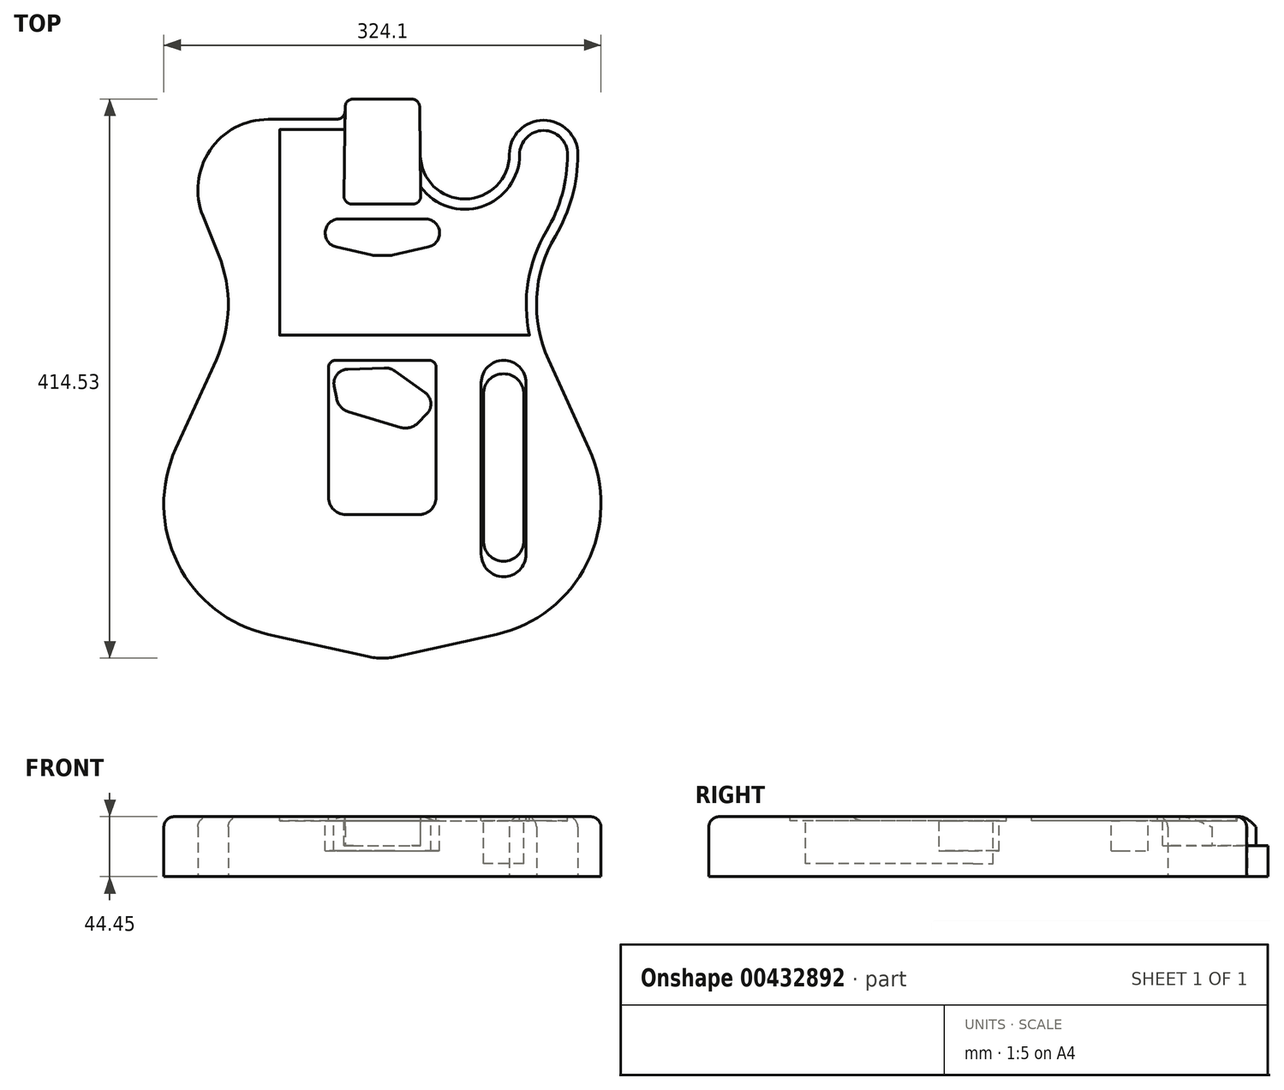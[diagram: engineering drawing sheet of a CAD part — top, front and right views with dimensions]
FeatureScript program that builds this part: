
annotation { "Feature Type Name" : "Feature", "Feature Type Description" : "" }
export const myFeature = defineFeature(function(context is Context, id is Id, definition is map)
    precondition{}
    {
        {
            var Q0;
            Q0=qCreatedBy(makeId("Top.planeOp"),FACE);
            var sketch = newSketch(context, id + "F0", { "sketchPlane" : qUnion([Q0])});
            skLineSegment(sketch, "E0", {"start": v(0, 414.53) * mm, "end": v(0, 0) * mm, "construction": true});
            skLineSegment(sketch, "E1", {"start": v(-27.56, 414.53) * mm, "end": v(27.56, 414.53) * mm});
            skPoint(sketch, "E2", {"position": v(0, 347.22) * mm});
            skLineSegment(sketch, "E3", {"start": v(28.1, 372.95) * mm, "end": v(27.56, 414.53) * mm});
            skArc(sketch, "E4", {"start": v(-153.14, 155.36) * mm, "mid": v(-151.67, 70.15) * mm, "end": v(-84.56, 17.62) * mm});
            skArc(sketch, "E5", {"start": v(-84.58, 399.42) * mm, "mid": v(-127.85, 376.42) * mm, "end": v(-133, 327.7) * mm});
            skLineSegment(sketch, "E6", {"start": v(-84.58, 347.22) * mm, "end": v(0, 347.22) * mm, "construction": true});
            skArc(sketch, "E7", {"start": v(28.1, 373.38) * mm, "mid": v(61.12, 340.36) * mm, "end": v(94.14, 373.38) * mm});
            skLineSegment(sketch, "E8", {"start": v(61.12, 373.38) * mm, "end": v(28.1, 373.38) * mm, "construction": true});
            skArc(sketch, "E9", {"start": v(144.94, 373.38) * mm, "mid": v(119.54, 398.78) * mm, "end": v(94.14, 373.38) * mm});
            skLineSegment(sketch, "E10", {"start": v(0, 262.13) * mm, "end": v(-114.3, 262.13) * mm, "construction": true});
            skArc(sketch, "E11", {"start": v(-123.21, 221.06) * mm, "mid": v(-114.32, 259.94) * mm, "end": v(-121.5, 299.18) * mm});
            skLineSegment(sketch, "E12", {"start": v(-133, 327.7) * mm, "end": v(-121.5, 299.18) * mm});
            skLineSegment(sketch, "E13", {"start": v(-123.21, 221.06) * mm, "end": v(-153.14, 155.36) * mm});
            skArc(sketch, "E14", {"start": v(84.56, 17.62) * mm, "mid": v(151.67, 70.15) * mm, "end": v(153.14, 155.36) * mm});
            skArc(sketch, "E15", {"start": v(128.27, 312.84) * mm, "mid": v(114.45, 267.57) * mm, "end": v(123.21, 221.06) * mm});
            skArc(sketch, "E16", {"start": v(144.94, 373.38) * mm, "mid": v(140.7, 341.98) * mm, "end": v(128.27, 312.84) * mm});
            skLineSegment(sketch, "E17", {"start": v(123.21, 221.06) * mm, "end": v(153.14, 155.36) * mm});
            skLineSegment(sketch, "E18", {"start": v(-84.58, 399.42) * mm, "end": v(-27.76, 399.42) * mm});
            skLineSegment(sketch, "E19.trimOffspring", {"start": v(-27.76, 399.41) * mm, "end": v(-27.56, 414.53) * mm});
            skArc(sketch, "E20", {"start": v(-11.06, 1.22) * mm, "mid": v(0, 0) * mm, "end": v(11.06, 1.22) * mm});
            skLineSegment(sketch, "E21", {"start": v(84.56, 17.62) * mm, "end": v(11.06, 1.22) * mm});
            skLineSegment(sketch, "E22", {"start": v(-84.56, 17.62) * mm, "end": v(-11.06, 1.22) * mm});
            skSolve(sketch);
        }
        {
            var Q0;
            Q0=makeQuery(id+"F0.imprint","IMPRINT",FACE,{"disambiguationData":[TD([[makeQuery(id+"F0.imprint","IMPRINT",EDGE,{"derivedFrom":sQuery(id+"F0.wireOp",EDGE,"E1")}),-1.0]])]});
            extrude(context, id + "F1", {"entities" : qUnion([Q0]), "depth" : 44.45 * mm});
        }
        {
            var Q0;
            Q0=makeQuery(id+"F1.opExtrude","SWEPT_EDGE",EDGE,{"disambiguationData":[OSD([sQuery(id+"F0.wireOp",EDGE,"E18"),sQuery(id+"F0.wireOp",EDGE,"E19.trimOffspring")])]});
            fillet(context, id + "F2", {"entities" : qUnion([Q0]), "radius" : 6.35 * mm, "tangentPropagation" : true, "allowEdgeOverflow" : false});
        }
        {
            var Q0;
            Q0=makeQuery(id+"F1.opExtrude","CAP_FACE",FACE,{"disambiguationData":[OSD([sQuery(id+"F0.wireOp",EDGE,"E1"),sQuery(id+"F0.wireOp",EDGE,"E3"),sQuery(id+"F0.wireOp",EDGE,"E4"),sQuery(id+"F0.wireOp",EDGE,"E5"),sQuery(id+"F0.wireOp",EDGE,"E7"),sQuery(id+"F0.wireOp",EDGE,"E9"),sQuery(id+"F0.wireOp",EDGE,"E11"),sQuery(id+"F0.wireOp",EDGE,"E12"),sQuery(id+"F0.wireOp",EDGE,"E13"),sQuery(id+"F0.wireOp",EDGE,"E14"),sQuery(id+"F0.wireOp",EDGE,"E15"),sQuery(id+"F0.wireOp",EDGE,"E16"),sQuery(id+"F0.wireOp",EDGE,"E17"),sQuery(id+"F0.wireOp",EDGE,"E18"),sQuery(id+"F0.wireOp",EDGE,"E19.trimOffspring"),sQuery(id+"F0.wireOp",EDGE,"E20"),sQuery(id+"F0.wireOp",EDGE,"E21"),sQuery(id+"F0.wireOp",EDGE,"E22")])],"isStart":false});
            var sketch = newSketch(context, id + "F3", { "sketchPlane" : qUnion([Q0])});
            skLineSegment(sketch, "E23", {"start": v(-27.56, 414.53) * mm, "end": v(27.56, 414.53) * mm});
            skLineSegment(sketch, "E24", {"start": v(-28.58, 336.55) * mm, "end": v(28.58, 336.55) * mm});
            skLineSegment(sketch, "E25", {"start": v(0, 414.53) * mm, "end": v(0, 0) * mm, "construction": true});
            skPoint(sketch, "E26", {"position": v(0, 336.55) * mm});
            skLineSegment(sketch, "E27", {"start": v(-27.56, 414.53) * mm, "end": v(-28.58, 336.55) * mm});
            skLineSegment(sketch, "E28", {"start": v(27.56, 414.53) * mm, "end": v(28.58, 336.55) * mm});
            skSolve(sketch);
        }
        {
            var Q0;
            Q0 = qSketchRegion(id + "F3", true);
            extrude(context, id + "F4", {"entities" : qUnion([Q0]), "operationType" : NewBodyOperationType.REMOVE, "oppositeDirection" : true, "depth" : 21.59 * mm});
        }
        {
            var Q0;
            Q0=makeQuery(id+"F4.boolean.opBoolean","COPY",EDGE,{"derivedFrom":makeQuery(id+"F4.opExtrude","SWEPT_EDGE",EDGE,{"disambiguationData":[OSD([sQuery(id+"F3.wireOp",EDGE,"E24"),sQuery(id+"F3.wireOp",EDGE,"E27")])]})});
            var Q1;
            Q1=makeQuery(id+"F1.opExtrude","SWEPT_EDGE",EDGE,{"disambiguationData":[OSD([sQuery(id+"F0.wireOp",EDGE,"E1"),sQuery(id+"F0.wireOp",EDGE,"E19.trimOffspring")])]});
            var Q2;
            Q2=makeQuery(id+"F1.opExtrude","SWEPT_EDGE",EDGE,{"disambiguationData":[OSD([sQuery(id+"F0.wireOp",EDGE,"E1"),sQuery(id+"F0.wireOp",EDGE,"E3")])]});
            var Q3;
            Q3=makeQuery(id+"F4.boolean.opBoolean","COPY",EDGE,{"derivedFrom":makeQuery(id+"F4.opExtrude","SWEPT_EDGE",EDGE,{"disambiguationData":[OSD([sQuery(id+"F3.wireOp",EDGE,"E24"),sQuery(id+"F3.wireOp",EDGE,"E28")])]})});
            fillet(context, id + "F5", {"entities" : qUnion([Q0, Q1, Q2, Q3]), "radius" : 6.02 * mm, "tangentPropagation" : true, "allowEdgeOverflow" : false});
        }
        {
            var Q0;
            Q0=makeQuery(id+"F1.opExtrude","CAP_FACE",FACE,{"disambiguationData":[OSD([sQuery(id+"F0.wireOp",EDGE,"E1"),sQuery(id+"F0.wireOp",EDGE,"E3"),sQuery(id+"F0.wireOp",EDGE,"E4"),sQuery(id+"F0.wireOp",EDGE,"E5"),sQuery(id+"F0.wireOp",EDGE,"E7"),sQuery(id+"F0.wireOp",EDGE,"E9"),sQuery(id+"F0.wireOp",EDGE,"E11"),sQuery(id+"F0.wireOp",EDGE,"E12"),sQuery(id+"F0.wireOp",EDGE,"E13"),sQuery(id+"F0.wireOp",EDGE,"E14"),sQuery(id+"F0.wireOp",EDGE,"E15"),sQuery(id+"F0.wireOp",EDGE,"E16"),sQuery(id+"F0.wireOp",EDGE,"E17"),sQuery(id+"F0.wireOp",EDGE,"E18"),sQuery(id+"F0.wireOp",EDGE,"E19.trimOffspring"),sQuery(id+"F0.wireOp",EDGE,"E20"),sQuery(id+"F0.wireOp",EDGE,"E21"),sQuery(id+"F0.wireOp",EDGE,"E22")])],"isStart":false});
            var sketch = newSketch(context, id + "F6", { "sketchPlane" : qUnion([Q0])});
            skLineSegment(sketch, "E29", {"start": v(0, 0) * mm, "end": v(0, 336.55) * mm, "construction": true});
            skLineSegment(sketch, "E30", {"start": v(-31.88, 325.63) * mm, "end": v(31.88, 325.63) * mm});
            skPoint(sketch, "E31", {"position": v(0, 325.63) * mm});
            skArc(sketch, "E32", {"start": v(-31.88, 325.63) * mm, "mid": v(-42.35, 316.27) * mm, "end": v(-34.22, 304.8) * mm});
            skLineSegment(sketch, "E33", {"start": v(0, 298.46) * mm, "end": v(-6.35, 298.46) * mm});
            skLineSegment(sketch, "E34", {"start": v(-6.35, 298.46) * mm, "end": v(-34.22, 304.8) * mm});
            skArc(sketch, "E35", {"start": v(34.22, 304.8) * mm, "mid": v(42.35, 316.27) * mm, "end": v(31.88, 325.63) * mm});
            skLineSegment(sketch, "E36", {"start": v(0, 298.46) * mm, "end": v(6.35, 298.46) * mm});
            skLineSegment(sketch, "E37", {"start": v(6.35, 298.46) * mm, "end": v(34.22, 304.8) * mm});
            skArc(sketch, "E38", {"start": v(-25.76, 214.24) * mm, "mid": v(-33.64, 210.29) * mm, "end": v(-35.75, 201.72) * mm});
            skArc(sketch, "E39", {"start": v(32.95, 181.11) * mm, "mid": v(35.9, 189.43) * mm, "end": v(31.5, 197.07) * mm});
            skLineSegment(sketch, "E40", {"start": v(-25.4, 203.7) * mm, "end": v(25.4, 188.47) * mm, "construction": true});
            skPoint(sketch, "E41", {"position": v(0, 196.09) * mm});
            skLineSegment(sketch, "E42", {"start": v(0, 196.09) * mm, "end": v(-5.77, 176.87) * mm, "construction": true});
            skLineSegment(sketch, "E43", {"start": v(-32.53, 184.9) * mm, "end": v(21, 168.84) * mm});
            skLineSegment(sketch, "E44", {"start": v(0, 196.09) * mm, "end": v(5.77, 215.3) * mm, "construction": true});
            skLineSegment(sketch, "E45", {"start": v(5.77, 215.3) * mm, "end": v(-25.76, 214.24) * mm});
            skLineSegment(sketch, "E46", {"start": v(5.77, 215.3) * mm, "end": v(31.5, 197.07) * mm});
            skLineSegment(sketch, "E47", {"start": v(-32.53, 184.9) * mm, "end": v(-35.75, 201.72) * mm});
            skLineSegment(sketch, "E48", {"start": v(21, 168.84) * mm, "end": v(32.95, 181.11) * mm});
            skSolve(sketch);
        }
        {
            var Q0;
            Q0=makeQuery(id+"F6.imprint","IMPRINT",FACE,{"disambiguationData":[TD([[makeQuery(id+"F6.imprint","IMPRINT",EDGE,{"derivedFrom":sQuery(id+"F6.wireOp",EDGE,"E30")}),-1.0]])]});
            var Q1;
            Q1=makeQuery(id+"F6.imprint","IMPRINT",FACE,{"disambiguationData":[TD([[makeQuery(id+"F6.imprint","IMPRINT",EDGE,{"derivedFrom":sQuery(id+"F6.wireOp",EDGE,"E38")}),1.0]])]});
            extrude(context, id + "F7", {"entities" : qUnion([Q0, Q1]), "operationType" : NewBodyOperationType.REMOVE, "oppositeDirection" : true, "depth" : 25.4 * mm});
        }
        {
            var Q0;
            Q0=makeQuery(id+"F1.opExtrude","CAP_FACE",FACE,{"disambiguationData":[OSD([sQuery(id+"F0.wireOp",EDGE,"E1"),sQuery(id+"F0.wireOp",EDGE,"E3"),sQuery(id+"F0.wireOp",EDGE,"E4"),sQuery(id+"F0.wireOp",EDGE,"E5"),sQuery(id+"F0.wireOp",EDGE,"E7"),sQuery(id+"F0.wireOp",EDGE,"E9"),sQuery(id+"F0.wireOp",EDGE,"E11"),sQuery(id+"F0.wireOp",EDGE,"E12"),sQuery(id+"F0.wireOp",EDGE,"E13"),sQuery(id+"F0.wireOp",EDGE,"E14"),sQuery(id+"F0.wireOp",EDGE,"E15"),sQuery(id+"F0.wireOp",EDGE,"E16"),sQuery(id+"F0.wireOp",EDGE,"E17"),sQuery(id+"F0.wireOp",EDGE,"E18"),sQuery(id+"F0.wireOp",EDGE,"E19.trimOffspring"),sQuery(id+"F0.wireOp",EDGE,"E20"),sQuery(id+"F0.wireOp",EDGE,"E21"),sQuery(id+"F0.wireOp",EDGE,"E22")])],"isStart":false});
            var sketch = newSketch(context, id + "F8", { "sketchPlane" : qUnion([Q0])});
            skArc(sketch, "E49", {"start": v(104.9, 195.83) * mm, "mid": v(89.92, 210.82) * mm, "end": v(74.93, 195.83) * mm});
            skLineSegment(sketch, "E50", {"start": v(0, 336.55) * mm, "end": v(0, 0) * mm, "construction": true});
            skArc(sketch, "E51", {"start": v(74.93, 86.87) * mm, "mid": v(89.92, 71.88) * mm, "end": v(104.9, 86.87) * mm});
            skLineSegment(sketch, "E52", {"start": v(74.93, 195.83) * mm, "end": v(74.93, 86.87) * mm});
            skLineSegment(sketch, "E53", {"start": v(104.9, 195.83) * mm, "end": v(104.9, 86.87) * mm});
            skSolve(sketch);
        }
        {
            var Q0;
            Q0=makeQuery(id+"F8.imprint","IMPRINT",FACE,{"disambiguationData":[TD([[makeQuery(id+"F8.imprint","IMPRINT",EDGE,{"derivedFrom":sQuery(id+"F8.wireOp",EDGE,"E49")}),1.0]])]});
            extrude(context, id + "F9", {"entities" : qUnion([Q0]), "operationType" : NewBodyOperationType.REMOVE, "oppositeDirection" : true, "depth" : 34.8 * mm});
        }
        {
            var Q0;
            Q0=makeQuery(id+"F1.opExtrude","CAP_FACE",FACE,{"disambiguationData":[OSD([sQuery(id+"F0.wireOp",EDGE,"E1"),sQuery(id+"F0.wireOp",EDGE,"E3"),sQuery(id+"F0.wireOp",EDGE,"E4"),sQuery(id+"F0.wireOp",EDGE,"E5"),sQuery(id+"F0.wireOp",EDGE,"E7"),sQuery(id+"F0.wireOp",EDGE,"E9"),sQuery(id+"F0.wireOp",EDGE,"E11"),sQuery(id+"F0.wireOp",EDGE,"E12"),sQuery(id+"F0.wireOp",EDGE,"E13"),sQuery(id+"F0.wireOp",EDGE,"E14"),sQuery(id+"F0.wireOp",EDGE,"E15"),sQuery(id+"F0.wireOp",EDGE,"E16"),sQuery(id+"F0.wireOp",EDGE,"E17"),sQuery(id+"F0.wireOp",EDGE,"E18"),sQuery(id+"F0.wireOp",EDGE,"E19.trimOffspring"),sQuery(id+"F0.wireOp",EDGE,"E20"),sQuery(id+"F0.wireOp",EDGE,"E21"),sQuery(id+"F0.wireOp",EDGE,"E22")])],"isStart":false});
            var sketch = newSketch(context, id + "F10", { "sketchPlane" : qUnion([Q0])});
            skArc(sketch, "E54.0", {"start": v(28.1, 372.95) * mm, "mid": v(61.33, 340.36) * mm, "end": v(94.14, 373.38) * mm, "construction": true});
            skArc(sketch, "E54.1", {"start": v(144.94, 373.38) * mm, "mid": v(119.54, 398.78) * mm, "end": v(94.14, 373.38) * mm, "construction": true});
            skArc(sketch, "E54.2", {"start": v(144.94, 373.38) * mm, "mid": v(140.7, 341.98) * mm, "end": v(128.27, 312.84) * mm, "construction": true});
            skArc(sketch, "E54.3", {"start": v(128.27, 312.84) * mm, "mid": v(114.45, 267.57) * mm, "end": v(123.21, 221.06) * mm, "construction": true});
            skArc(sketch, "E55.0", {"start": v(121.72, 316.74) * mm, "mid": v(108.07, 279.27) * mm, "end": v(109.13, 239.4) * mm});
            skArc(sketch, "E55.1", {"start": v(137.32, 373.38) * mm, "mid": v(133.35, 344) * mm, "end": v(121.72, 316.74) * mm});
            skArc(sketch, "E55.2", {"start": v(137.32, 373.38) * mm, "mid": v(119.54, 391.16) * mm, "end": v(101.76, 373.38) * mm});
            skArc(sketch, "E55.3", {"start": v(28.4, 349.26) * mm, "mid": v(73.81, 334.77) * mm, "end": v(101.76, 373.38) * mm});
            skLineSegment(sketch, "E56.0", {"start": v(28.4, 349.26) * mm, "end": v(28.5, 342.65) * mm});
            skArc(sketch, "E56.1", {"start": v(28.5, 342.65) * mm, "mid": v(26.76, 338.34) * mm, "end": v(22.48, 336.55) * mm});
            skLineSegment(sketch, "E56.2", {"start": v(-22.48, 336.55) * mm, "end": v(22.48, 336.55) * mm});
            skArc(sketch, "E56.3", {"start": v(-22.48, 336.55) * mm, "mid": v(-26.76, 338.34) * mm, "end": v(-28.5, 342.65) * mm});
            skLineSegment(sketch, "E56.4", {"start": v(-28.5, 342.65) * mm, "end": v(-27.86, 391.8) * mm});
            skLineSegment(sketch, "E57", {"start": v(-27.86, 391.8) * mm, "end": v(-76.2, 391.8) * mm});
            skLineSegment(sketch, "E58", {"start": v(0, 0) * mm, "end": v(0, 336.55) * mm, "construction": true});
            skLineSegment(sketch, "E59", {"start": v(-76.2, 391.8) * mm, "end": v(-76.2, 239.4) * mm});
            skLineSegment(sketch, "E60", {"start": v(-76.2, 239.4) * mm, "end": v(109.13, 239.4) * mm});
            skLineSegment(sketch, "E61.bottom", {"start": v(39.88, 220.73) * mm, "end": v(-39.88, 220.73) * mm});
            skLineSegment(sketch, "E61.top", {"start": v(39.88, 106.43) * mm, "end": v(-39.88, 106.43) * mm});
            skLineSegment(sketch, "E61.left", {"start": v(39.88, 220.73) * mm, "end": v(39.88, 106.43) * mm});
            skLineSegment(sketch, "E61.right", {"start": v(-39.88, 220.73) * mm, "end": v(-39.88, 106.43) * mm});
            skPoint(sketch, "E61.middle", {"position": v(0, 163.58) * mm});
            skLineSegment(sketch, "E62", {"start": v(89.92, 210.82) * mm, "end": v(89.92, 71.88) * mm, "construction": true});
            skArc(sketch, "E63", {"start": v(106.55, 204.09) * mm, "mid": v(89.92, 220.73) * mm, "end": v(73.28, 204.09) * mm});
            skLineSegment(sketch, "E64", {"start": v(39.88, 220.73) * mm, "end": v(89.92, 220.73) * mm});
            skArc(sketch, "E65", {"start": v(73.28, 77.09) * mm, "mid": v(89.92, 60.45) * mm, "end": v(106.55, 77.09) * mm});
            skLineSegment(sketch, "E66", {"start": v(73.28, 204.09) * mm, "end": v(73.28, 77.09) * mm});
            skLineSegment(sketch, "E67", {"start": v(106.55, 77.09) * mm, "end": v(106.55, 204.09) * mm});
            skSolve(sketch);
        }
        {
            var Q0;
            Q0=makeQuery(id+"F10.imprint","IMPRINT",FACE,{"disambiguationData":[TD([[makeQuery(id+"F10.imprint","IMPRINT",EDGE,{"derivedFrom":sQuery(id+"F10.wireOp",EDGE,"E55.0")}),-1.0]])]});
            var Q1;
            Q1=makeQuery(id+"F10.imprint","IMPRINT",FACE,{"disambiguationData":[TD([[makeQuery(id+"F10.imprint","IMPRINT",EDGE,{"derivedFrom":sQuery(id+"F10.wireOp",EDGE,"E61.bottom")}),1.0]])]});
            var Q2;
            Q2=makeQuery(id+"F10.imprint","IMPRINT",FACE,{"disambiguationData":[TD([[makeQuery(id+"F10.imprint","IMPRINT",EDGE,{"derivedFrom":sQuery(id+"F10.wireOp",EDGE,"E65")}),1.0]])]});
            extrude(context, id + "F11", {"entities" : qUnion([Q0, Q1, Q2]), "operationType" : NewBodyOperationType.REMOVE, "oppositeDirection" : true, "depth" : 3.05 * mm});
        }
        {
            var Q0;
            Q0=makeQuery(id+"F11.boolean.opBoolean","COPY",EDGE,{"derivedFrom":makeQuery(id+"F11.opExtrude","SWEPT_EDGE",EDGE,{"disambiguationData":[OSD([sQuery(id+"F10.wireOp",EDGE,"E57"),sQuery(id+"F10.wireOp",EDGE,"E59")])]})});
            var Q1;
            Q1=makeQuery(id+"F11.boolean.opBoolean","COPY",EDGE,{"derivedFrom":makeQuery(id+"F11.opExtrude","SWEPT_EDGE",EDGE,{"disambiguationData":[OSD([sQuery(id+"F10.wireOp",EDGE,"E59"),sQuery(id+"F10.wireOp",EDGE,"E60")])]})});
            var Q2;
            Q2=makeQuery(id+"F11.boolean.opBoolean","COPY",EDGE,{"derivedFrom":makeQuery(id+"F11.opExtrude","SWEPT_EDGE",EDGE,{"disambiguationData":[OSD([sQuery(id+"F10.wireOp",EDGE,"E55.0"),sQuery(id+"F10.wireOp",EDGE,"E60")])]})});
            fillet(context, id + "F12", {"entities" : qUnion([Q0, Q1, Q2]), "radius" : 1.38 / 50.8 * mm, "tangentPropagation" : true, "allowEdgeOverflow" : false});
        }
        {
            var Q0;
            Q0=makeQuery(id+"F7.boolean.opBoolean","COPY",EDGE,{"derivedFrom":makeQuery(id+"F7.opExtrude","SWEPT_EDGE",EDGE,{"disambiguationData":[OSD([sQuery(id+"F6.wireOp",EDGE,"E43"),sQuery(id+"F6.wireOp",EDGE,"E47")])]})});
            var Q1;
            Q1=makeQuery(id+"F7.boolean.opBoolean","COPY",EDGE,{"derivedFrom":makeQuery(id+"F7.opExtrude","SWEPT_EDGE",EDGE,{"disambiguationData":[OSD([sQuery(id+"F6.wireOp",EDGE,"E45"),sQuery(id+"F6.wireOp",EDGE,"E46")])]})});
            var Q2;
            Q2=makeQuery(id+"F7.boolean.opBoolean","COPY",EDGE,{"derivedFrom":makeQuery(id+"F7.opExtrude","SWEPT_EDGE",EDGE,{"disambiguationData":[OSD([sQuery(id+"F6.wireOp",EDGE,"E43"),sQuery(id+"F6.wireOp",EDGE,"E48")])]})});
            var Q3;
            Q3=makeQuery(id+"F7.boolean.opBoolean","COPY",EDGE,{"derivedFrom":makeQuery(id+"F7.opExtrude","SWEPT_EDGE",EDGE,{"disambiguationData":[OSD([sQuery(id+"F6.wireOp",EDGE,"E33"),sQuery(id+"F6.wireOp",EDGE,"E34")])]})});
            var Q4;
            Q4=makeQuery(id+"F7.boolean.opBoolean","COPY",EDGE,{"derivedFrom":makeQuery(id+"F7.opExtrude","SWEPT_EDGE",EDGE,{"disambiguationData":[OSD([sQuery(id+"F6.wireOp",EDGE,"E36"),sQuery(id+"F6.wireOp",EDGE,"E37")])]})});
            fillet(context, id + "F13", {"entities" : qUnion([Q0, Q1, Q2, Q3, Q4]), "radius" : 12.7 * mm, "tangentPropagation" : true, "allowEdgeOverflow" : false});
        }
        {
            var Q0;
            Q0=makeQuery(id+"F11.boolean.opBoolean","COPY",EDGE,{"derivedFrom":makeQuery(id+"F11.opExtrude","SWEPT_EDGE",EDGE,{"disambiguationData":[OSD([sQuery(id+"F10.wireOp",EDGE,"E61.bottom"),sQuery(id+"F10.wireOp",EDGE,"E61.right")])]})});
            var Q1;
            Q1=makeQuery(id+"F11.boolean.opBoolean","COPY",EDGE,{"derivedFrom":makeQuery(id+"F11.opExtrude","SWEPT_EDGE",EDGE,{"disambiguationData":[OSD([sQuery(id+"F10.wireOp",EDGE,"E61.bottom"),sQuery(id+"F10.wireOp",EDGE,"E61.left")])]})});
            fillet(context, id + "F14", {"entities" : qUnion([Q0, Q1]), "radius" : 5.08 * mm, "tangentPropagation" : true, "allowEdgeOverflow" : false});
        }
        {
            var Q0;
            Q0=makeQuery(id+"F11.boolean.opBoolean","COPY",EDGE,{"derivedFrom":makeQuery(id+"F11.opExtrude","SWEPT_EDGE",EDGE,{"disambiguationData":[OSD([sQuery(id+"F10.wireOp",EDGE,"E61.top"),sQuery(id+"F10.wireOp",EDGE,"E61.right")])]})});
            var Q1;
            Q1=makeQuery(id+"F11.boolean.opBoolean","COPY",EDGE,{"derivedFrom":makeQuery(id+"F11.opExtrude","SWEPT_EDGE",EDGE,{"disambiguationData":[OSD([sQuery(id+"F10.wireOp",EDGE,"E61.top"),sQuery(id+"F10.wireOp",EDGE,"E61.left")])]})});
            fillet(context, id + "F15", {"entities" : qUnion([Q0, Q1]), "radius" : 12.7 * mm, "tangentPropagation" : true, "allowEdgeOverflow" : false});
        }
        {
            var Q0;
            Q0=makeQuery(id+"F11.boolean.opBoolean","COPY",EDGE,{"derivedFrom":makeQuery(id+"F11.opExtrude","CAP_EDGE",EDGE,{"disambiguationData":[OSD([sQuery(id+"F10.wireOp",EDGE,"E61.top")])],"isStart":false})});
            fillet(context, id + "F16", {"entities" : qUnion([Q0]), "radius" : 12.7 * mm, "allowEdgeOverflow" : false});
        }
        {
            var Q0;
            Q0=makeQuery(id+"F1.opExtrude","CAP_EDGE",EDGE,{"disambiguationData":[OSD([sQuery(id+"F0.wireOp",EDGE,"E5")])],"isStart":false});
            fillet(context, id + "F17", {"entities" : qUnion([Q0]), "radius" : 7.62 * mm, "tangentPropagation" : true, "allowEdgeOverflow" : false});
        }
    });
